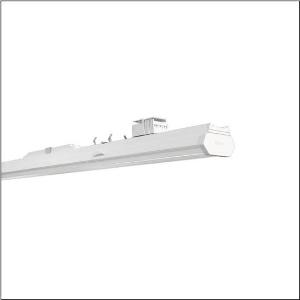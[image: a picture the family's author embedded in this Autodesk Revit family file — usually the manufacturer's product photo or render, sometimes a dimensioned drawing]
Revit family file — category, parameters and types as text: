
# Revit family: licross_11_protected_ho_51tp13dn4f5s
name_source: partatom
category: Lighting Fixtures
units: mm (PartAtom-declared; Revit-internal decimal feet)

## family parameters
Cut with Voids When Loaded = No
Host = Face
Light Source = No
Part Type = Normal
Room Calculation Point = No
Round Connector Dimension = Use Diameter
Shared = No

## types (1)
- --- (1 x LED, 15550 lm, 87.3 W, 4000K)
    Apparent Load = 87 VA
    CIE Flux Codes = 89 96 99 100 99
    Color Rendering = 80
    Color Temperature = 4000K
    Default Elevation = 1800 mm
    Description = Licross 11 Protected HO, luminaire insert, of sheet steel, galvanised, coil coated, white, length: 1.500mm, width: 90mm, height: 101mm, LED rated luminous flux: 15.550lm, light colour: 840, SDCM (Standard Deviation of Colour Matching)MacAdam ≤ 2 SDCM (initial), control gear: DALI 2, with plug, 5-pole, with phase selection, mains connection: 220..240V, AC, 50/60Hz, rated input power: 87W, internal wiring halogen-free, primary light control with lens, of plastic, primary optical cover: cover, of PMMA, light emission: direct distribution, primary light characteristic: symmetric, protection rating (complete): IP64, insulation class (complete): insulation class I (protective earthing), certification: CE, ENEC, VDE, UKCA, protection symbol: D if used in an environment with conductive dust loads with corresponding accessories, impact resistance: IK06, permissible ambient temperature for indoor applications: -25..+30°C, corresponds to IFS (International Featured Standards) requirements for safety and quality in the food industry, reducing of maximum allowable ambient temperature of 5°C with ceiling mounting, LABS conformity tested according to VDMA 24364:2018-05, The light source and the operating device comply with the requirements of the Ecodesign Regulation (EU) 2019/2020 and are replaceable in accordance with this regulation, packaging unit: 1 piece
    Height = 92 mm
    Lamp = 1 x LED
    Lamp Light Flux = 15550 lm
    Lamp Power = 87.3 W
    Lamp count = 1
    Length = 1500 mm
    Luminous efficacy = 178 lm/W
    Manufacturer = Siteco
    ModVariant = No
    Model = 51TP13DN4F5S
    Mounting Place = Ceiling
    Mounting Type = Pendant
    Number of Poles = 1
    OnlyDefault = Yes
    Power Factor = 1
    Product Name = Licross 11 Protected HO
    Product group = luminaire insert | ceiling pendant
    ProductGroupID = 901
    Protection Class = Protection class I
    Protection Degree = IP 64
    RLX_Detail_Level = 1
    RLX_Emergency_Light_Flux = 0 lm
    RLX_Emergency_Type = 0
    RLX_Emergency_Type_DB = No
    RlxData = <blob elided: 24533 chars, md5=b151342c>
    Socket = socket
    Standby Power = 0 W
    System Light Flux = 15550 lm
    System Power = 87 W
    Type Comments = factory setting: luminous flux: 100 % | dim-lin: 254 | 589 mA
    Type Image = l_1256148.jpg
    URL = http://relux.com
    VarID = @adj_103987
    Voltage = 0 V
    Weight = 0.00 kg
    Width = 88 mm

## geometry (parser evidence)
native form markers: Blend x4, Sweep x10
no freeform markers — native parametric forms only
